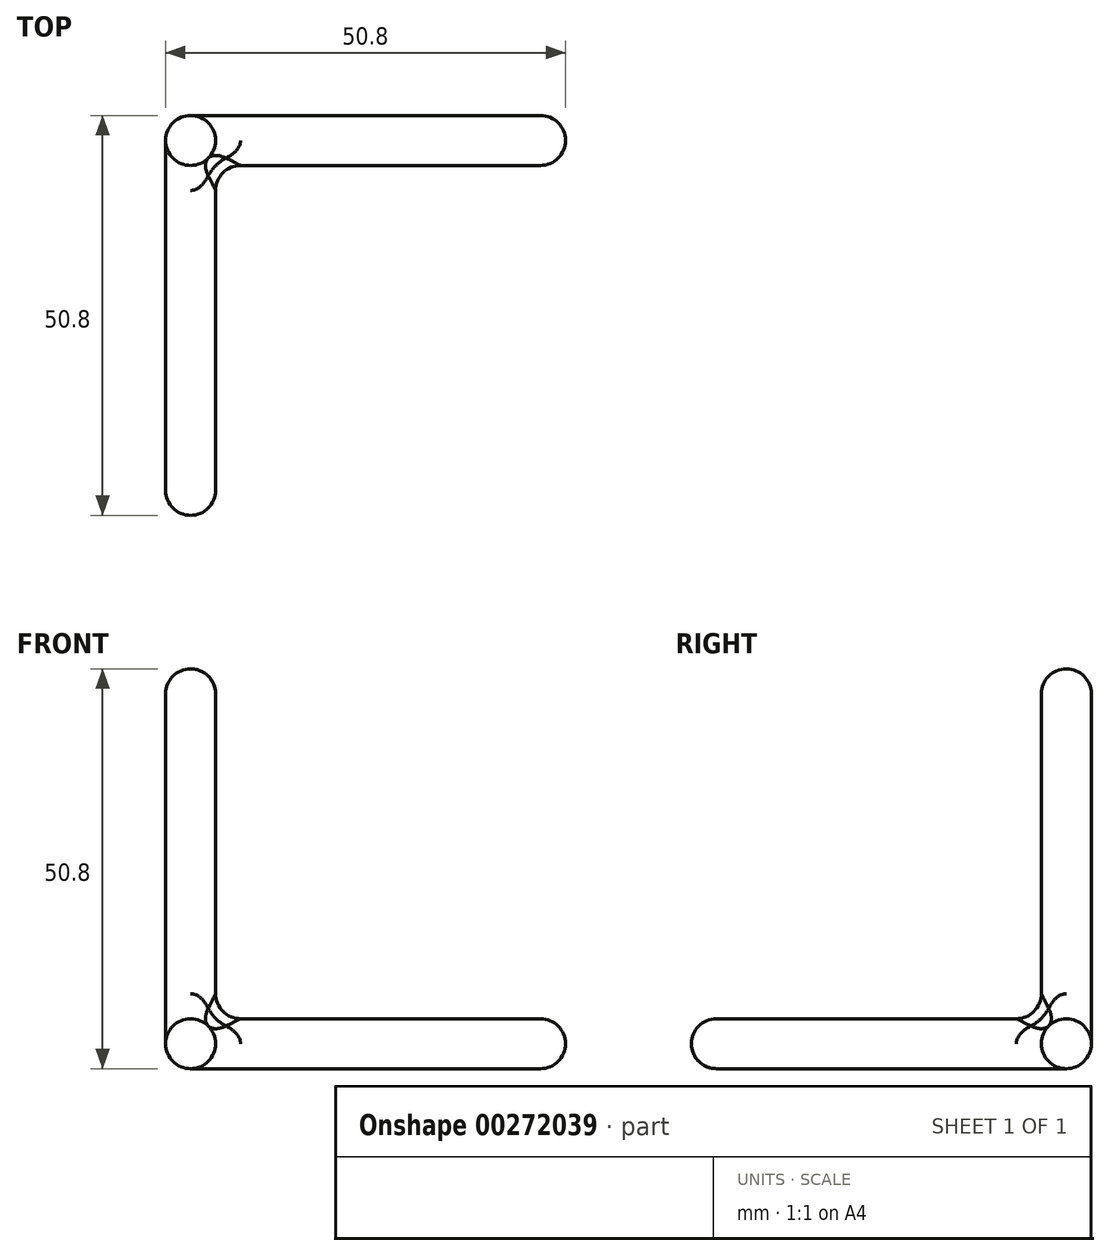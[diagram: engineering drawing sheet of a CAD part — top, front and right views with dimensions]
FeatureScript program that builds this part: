
annotation { "Feature Type Name" : "Feature", "Feature Type Description" : "" }
export const myFeature = defineFeature(function(context is Context, id is Id, definition is map)
    precondition{}
    {
        {
            var Q0;
            Q0=qCreatedBy(makeId("Front.planeOp"),FACE);
            var sketch = newSketch(context, id + "F0", { "sketchPlane" : qUnion([Q0])});
            skLineSegment(sketch, "E0.bottom", {"start": v(0, 0) * mm, "end": v(6.35, 0) * mm});
            skLineSegment(sketch, "E0.top", {"start": v(0, 50.8) * mm, "end": v(6.35, 50.8) * mm});
            skLineSegment(sketch, "E0.left", {"start": v(0, 0) * mm, "end": v(0, 50.8) * mm});
            skLineSegment(sketch, "E0.right", {"start": v(6.35, 0) * mm, "end": v(6.35, 50.8) * mm});
            skLineSegment(sketch, "E1.bottom", {"start": v(0, 0) * mm, "end": v(50.8, 0) * mm});
            skLineSegment(sketch, "E1.top", {"start": v(0, 6.35) * mm, "end": v(50.8, 6.35) * mm});
            skLineSegment(sketch, "E1.left", {"start": v(0, 0) * mm, "end": v(0, 6.35) * mm});
            skLineSegment(sketch, "E1.right", {"start": v(50.8, 0) * mm, "end": v(50.8, 6.35) * mm});
            skSolve(sketch);
        }
        {
            var Q0;
            Q0 = qSketchRegion(id + "F0", true);
            extrude(context, id + "F1", {"entities" : qUnion([Q0]), "endBound" : BoundingType.SYMMETRIC, "depth" : 6.35 * mm});
        }
        {
            var Q0;
            Q0=makeQuery(id+"F1.opExtrude","CAP_FACE",FACE,{"disambiguationData":[OSD([sQuery(id+"F0.wireOp",EDGE,"E0.top"),sQuery(id+"F0.wireOp",EDGE,"E0.left"),sQuery(id+"F0.wireOp",EDGE,"E0.right"),sQuery(id+"F0.wireOp",EDGE,"E1.bottom"),sQuery(id+"F0.wireOp",EDGE,"E1.top"),sQuery(id+"F0.wireOp",EDGE,"E1.left"),sQuery(id+"F0.wireOp",EDGE,"E1.right")])],"isStart":true});
            var sketch = newSketch(context, id + "F2", { "sketchPlane" : qUnion([Q0])});
            skLineSegment(sketch, "E2.bottom", {"start": v(0, 0) * mm, "end": v(-6.35, 0) * mm});
            skLineSegment(sketch, "E2.top", {"start": v(0, 6.35) * mm, "end": v(-6.35, 6.35) * mm});
            skLineSegment(sketch, "E2.left", {"start": v(0, 0) * mm, "end": v(0, 6.35) * mm});
            skLineSegment(sketch, "E2.right", {"start": v(-6.35, 0) * mm, "end": v(-6.35, 6.35) * mm});
            skSolve(sketch);
        }
        {
            var Q0;
            Q0 = qSketchRegion(id + "F2", true);
            extrude(context, id + "F3", {"entities" : qUnion([Q0]), "operationType" : NewBodyOperationType.ADD, "oppositeDirection" : true, "depth" : 50.8 * mm});
        }
        {
            var Q0;
            {var subQ0=sQuery(id+"F0.wireOp",EDGE,"E0.right");var subQ1=sQuery(id+"F0.wireOp",EDGE,"E1.left");var subQ2=sQuery(id+"F0.wireOp",EDGE,"E0.left");var subQ3=sQuery(id+"F0.wireOp",EDGE,"E1.top");var subQ4=sQuery(id+"F0.wireOp",EDGE,"E0.top");var subQ5=makeQuery(id+"F1.opExtrude","CAP_FACE",FACE,{"disambiguationData":[OSD([subQ4,subQ2,subQ0,sQuery(id+"F0.wireOp",EDGE,"E1.bottom"),subQ3,subQ1,sQuery(id+"F0.wireOp",EDGE,"E1.right")])],"isStart":false});Q0=makeQuery(id+"F3.boolean.opBoolean","SPLIT",FACE,{"disambiguationData":[TD([makeQuery(id+"F1.opExtrude","SWEPT_FACE",FACE,{"disambiguationData":[OSD([subQ4])]})])],"derivedFrom":subQ5});}
            var Q1;
            Q1=makeQuery(id+"F3.opExtrude","SWEPT_FACE",FACE,{"disambiguationData":[OSD([sQuery(id+"F2.wireOp",EDGE,"E2.top")])]});
            var Q2;
            Q2=makeQuery(id+"F3.opExtrude","SWEPT_FACE",FACE,{"disambiguationData":[OSD([sQuery(id+"F2.wireOp",EDGE,"E2.right")])]});
            var Q3;
            Q3=makeQuery(id+"F1.opExtrude","SWEPT_FACE",FACE,{"disambiguationData":[OSD([sQuery(id+"F0.wireOp",EDGE,"E0.right")])]});
            var Q4;
            Q4=makeQuery(id+"F1.opExtrude","CAP_EDGE",EDGE,{"disambiguationData":[OSD([sQuery(id+"F0.wireOp",EDGE,"E1.top")])],"isStart":true});
            var Q5;
            {var subQ0=sQuery(id+"F0.wireOp",EDGE,"E1.top");var subQ1=sQuery(id+"F0.wireOp",EDGE,"E1.bottom");var subQ2=sQuery(id+"F0.wireOp",EDGE,"E0.right");var subQ3=sQuery(id+"F0.wireOp",EDGE,"E1.right");var subQ4=makeQuery(id+"F1.opExtrude","CAP_FACE",FACE,{"disambiguationData":[OSD([sQuery(id+"F0.wireOp",EDGE,"E0.top"),sQuery(id+"F0.wireOp",EDGE,"E0.left"),subQ2,subQ1,subQ0,sQuery(id+"F0.wireOp",EDGE,"E1.left"),subQ3])],"isStart":false});Q5=makeQuery(id+"F3.boolean.opBoolean","SPLIT",FACE,{"disambiguationData":[TD([makeQuery(id+"F1.opExtrude","SWEPT_FACE",FACE,{"disambiguationData":[OSD([subQ1])]})])],"derivedFrom":subQ4});}
            var Q6;
            Q6=makeQuery(id+"F3.boolean.opBoolean","MERGE",FACE,{"derivedFrom":[makeQuery(id+"F1.opExtrude","SWEPT_FACE",FACE,{"disambiguationData":[OSD([sQuery(id+"F0.wireOp",EDGE,"E1.bottom")])]}),makeQuery(id+"F3.opExtrude","SWEPT_FACE",FACE,{"disambiguationData":[OSD([sQuery(id+"F2.wireOp",EDGE,"E2.bottom")])]})]});
            var Q7;
            Q7=makeQuery(id+"F3.boolean.opBoolean","MERGE",FACE,{"derivedFrom":[makeQuery(id+"F1.opExtrude","SWEPT_FACE",FACE,{"disambiguationData":[OSD([sQuery(id+"F0.wireOp",EDGE,"E0.left"),sQuery(id+"F0.wireOp",EDGE,"E1.left")])]}),makeQuery(id+"F3.opExtrude","SWEPT_FACE",FACE,{"disambiguationData":[OSD([sQuery(id+"F2.wireOp",EDGE,"E2.left")])]})]});
            var Q8;
            Q8=makeQuery(id+"F1.opExtrude","CAP_FACE",FACE,{"disambiguationData":[OSD([sQuery(id+"F0.wireOp",EDGE,"E0.top"),sQuery(id+"F0.wireOp",EDGE,"E0.left"),sQuery(id+"F0.wireOp",EDGE,"E0.right"),sQuery(id+"F0.wireOp",EDGE,"E1.bottom"),sQuery(id+"F0.wireOp",EDGE,"E1.top"),sQuery(id+"F0.wireOp",EDGE,"E1.left"),sQuery(id+"F0.wireOp",EDGE,"E1.right")])],"isStart":true});
            var Q9;
            Q9=makeQuery(id+"F1.opExtrude","SWEPT_FACE",FACE,{"disambiguationData":[OSD([sQuery(id+"F0.wireOp",EDGE,"E1.top")])]});
            fillet(context, id + "F4", {"entities" : qUnion([Q0, Q1, Q2, Q3, Q4, Q5, Q6, Q7, Q8, Q9]), "radius" : 3.17 * mm, "tangentPropagation" : true, "allowEdgeOverflow" : false});
        }
    });
